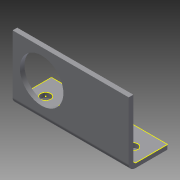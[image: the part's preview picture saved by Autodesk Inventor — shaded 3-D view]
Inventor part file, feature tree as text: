
AUTODESK INVENTOR PART (.ipt)
format: ipt  version: 2013 (Build 170138000, 138)  size: 216,576 bytes
history: native  units: in
note: dims shown in document units (in); Inventor stores cm internally (conversion verified against a paired STEP export)
features: sketch x9, other x7, reference x6, sheet_metal_op x4, extrude x3, projected_geometry x1
ambient origin geometry x8: Origin, YZ Plane, XZ Plane, XY Plane, X Axis, Y Axis, Z Axis, Center Point
bodies: Solid1 (feature_tree)
feature tree (30):
  sheet_metal_op  "Face1"
  sheet_metal_op  "Flange1"
  sketch  "Sketch9"  dims[d9=0.12in]
  sketch  "Sketch10"  dims[d10=0.0in]
  extrude  "Extrusion1"  Depth=1.5in
  extrude  "Extrusion2"  Depth=0.75in
  extrude  "Extrusion3"  Depth=0.75in
  sketch  "Sketch12"  dims[d12=0.06in]
  sketch  "Sketch13"  dims[d13=0.24in d14=0.12in d15=1.0in d16=90.0deg d17=0.05in d18=0.48in d19=0.12in d20=0.12in d32=0.12in d33=0.0in d34=1.5in d35=0.0in d36=1.5in d37=0.0in d38=1.5in d39=0.0in d40=0.12in d41=0.0in d42=0.12in d43=0.0in d5=0.0in]
  sketch  "Sketch1"  dims[d0=1.5in d1=1.5in]
  other  "Plate1"
  sketch  "Sketch2"  dims[d2=0.75in d3=0.75in]
  sketch  "Sketch3"  dims[d4=0.12in d7=0.75in]
  other  "Plate2"
  sheet_metal_op  "Bend1"
  sheet_metal_op  "Corner1"
  sketch  "Sketch8"  dims[d8=1.125in]
  reference  "Reference4"
  reference  "Reference5"
  reference  "Reference6"
  sketch  "Sketch11"  dims[d11=0.12in]
  reference  "Reference7"
  reference  "Reference8"
  projected_geometry  "Projected Loop1"
  reference  "Reference9"
  other  "Cut1"
  other  "Cut5"
  other  "Cut6"
  other  "Cut7"
  other  "Definition1"
